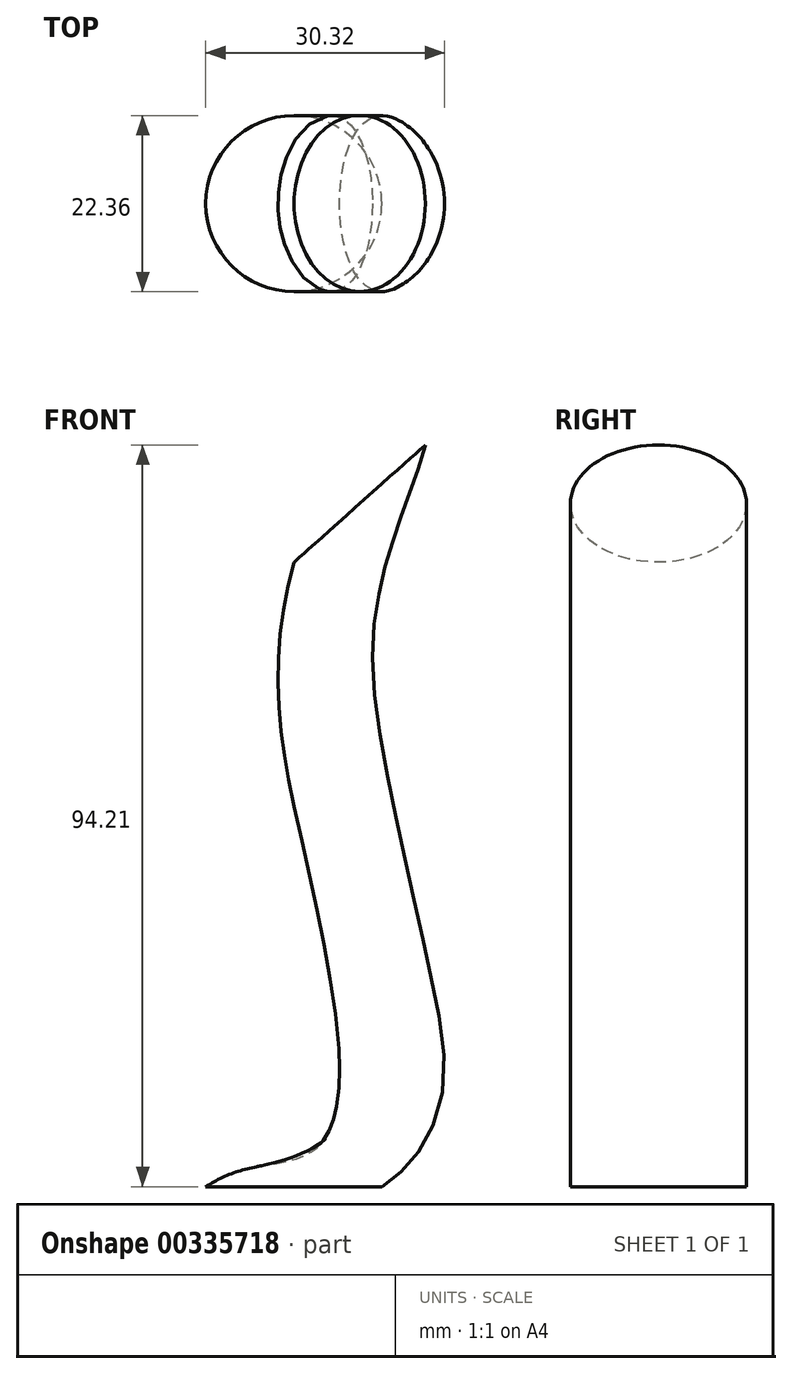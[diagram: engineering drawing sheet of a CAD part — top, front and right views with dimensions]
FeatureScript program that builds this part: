
annotation { "Feature Type Name" : "Feature", "Feature Type Description" : "" }
export const myFeature = defineFeature(function(context is Context, id is Id, definition is map)
    precondition{}
    {
        {
            var Q0;
            Q0=qCreatedBy(makeId("Top.planeOp"),FACE);
            var sketch = newSketch(context, id + "F0", { "sketchPlane" : qUnion([Q0])});
            skCircle(sketch, "E0", {"center": v(-62.28, 52.52) * mm, "radius": 11.18 * mm});
            skLineSegment(sketch, "E1", {"start": v(-82.91, 71.7) * mm, "end": v(-82.91, 30.26) * mm, "construction": true});
            skSolve(sketch);
        }
        {
            var Q0;
            Q0=sQuery(id+"F0.wireOp",VERTEX,"E0.center");
            var Q1;
            Q1=qCreatedBy(makeId("Front.planeOp"),FACE);
            cPlane(context, id + "F1", {"entities" : qUnion([Q0, Q1]), "cplaneType" : CPlaneType.PLANE_POINT, "offset" : 25.4 * mm, "width" : 152.4 * mm, "height" : 152.4 * mm});
        }
        {
            var Q0;
            Q0=qCreatedBy(id+"F1.planeOp",FACE);
            var sketch = newSketch(context, id + "F2", { "sketchPlane" : qUnion([Q0])});
            skFitSpline(sketch, "E2", {"points": [v(-62.62, 0) * mm, v(-51.8, 12.5) * mm, v(-57.55, 59.5) * mm, v(-54.17, 86.54) * mm], "startDerivative": vector(55.92, 35.8) * mm, "endDerivative": vector(20.35, 72.92) * mm});
            skSolve(sketch);
        }
        {
            var Q0;
            Q0=makeQuery(id+"F0.imprint","IMPRINT",FACE,{"disambiguationData":[TD([[makeQuery(id+"F0.imprint","IMPRINT",EDGE,{"derivedFrom":sQuery(id+"F0.wireOp",EDGE,"E0")}),1.0]])]});
            var Q1;
            Q1=sQuery(id+"F2.wireOp",EDGE,"E2");
            sweep(context, id + "F3", {"profiles" : qUnion([Q0]), "path" : qUnion([Q1])});
        }
    });
